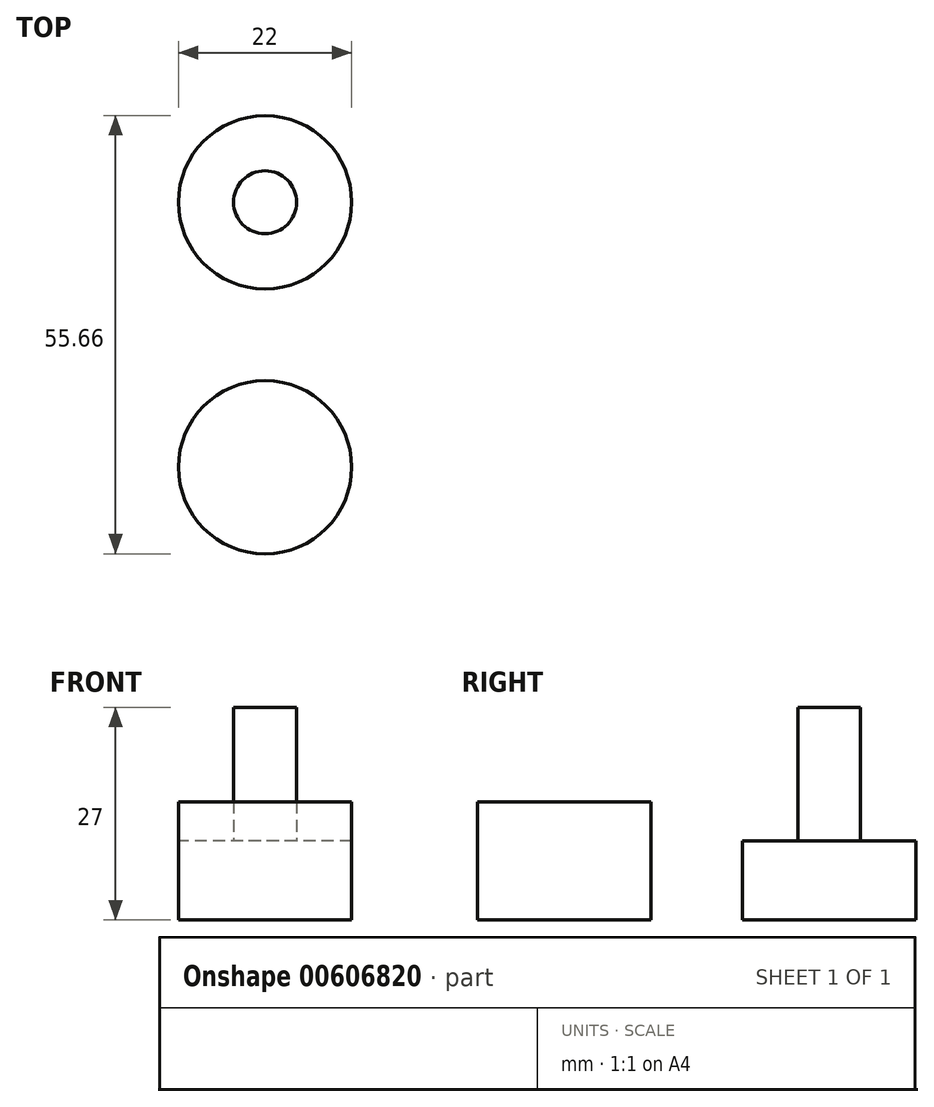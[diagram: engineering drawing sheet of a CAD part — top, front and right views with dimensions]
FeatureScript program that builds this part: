
annotation { "Feature Type Name" : "Feature", "Feature Type Description" : "" }
export const myFeature = defineFeature(function(context is Context, id is Id, definition is map)
    precondition{}
    {
        {
            var Q0;
            Q0=qCreatedBy(makeId("Top.planeOp"),FACE);
            var sketch = newSketch(context, id + "F0", { "sketchPlane" : qUnion([Q0])});
            skCircle(sketch, "E0", {"center": v(0, 0) * mm, "radius": 11 * mm});
            skSolve(sketch);
        }
        {
            var Q0;
            Q0=makeQuery(id+"F0.imprint","IMPRINT",FACE,{"disambiguationData":[TD([[makeQuery(id+"F0.imprint","IMPRINT",EDGE,{"derivedFrom":sQuery(id+"F0.wireOp",EDGE,"E0")}),1.0]])]});
            extrude(context, id + "F1", {"entities" : qUnion([Q0]), "depth" : 10 * mm, "offsetDistance" : 25 * mm});
        }
        {
            var Q0;
            Q0=makeQuery(id+"F1.opExtrude","CAP_FACE",FACE,{"disambiguationData":[OSD([sQuery(id+"F0.wireOp",EDGE,"E0")])],"isStart":false});
            var sketch = newSketch(context, id + "F2", { "sketchPlane" : qUnion([Q0])});
            skCircle(sketch, "E1", {"center": v(0, 0) * mm, "radius": 4 * mm});
            skSolve(sketch);
        }
        {
            var Q0;
            Q0 = qSketchRegion(id + "F2", true);
            extrude(context, id + "F3", {"entities" : qUnion([Q0]), "operationType" : NewBodyOperationType.ADD, "depth" : 17 * mm, "offsetDistance" : 25 * mm});
        }
        {
            var Q0;
            Q0=qCreatedBy(makeId("Top.planeOp"),FACE);
            var sketch = newSketch(context, id + "F4", { "sketchPlane" : qUnion([Q0])});
            skCircle(sketch, "E2", {"center": v(0, -33.66) * mm, "radius": 11 * mm});
            skSolve(sketch);
        }
        {
            var Q0;
            Q0=makeQuery(id+"F4.imprint","IMPRINT",FACE,{"disambiguationData":[TD([[makeQuery(id+"F4.imprint","IMPRINT",EDGE,{"derivedFrom":sQuery(id+"F4.wireOp",EDGE,"E2")}),1.0]])]});
            extrude(context, id + "F5", {"entities" : qUnion([Q0]), "depth" : 15 * mm, "offsetDistance" : 25 * mm});
        }
    });
